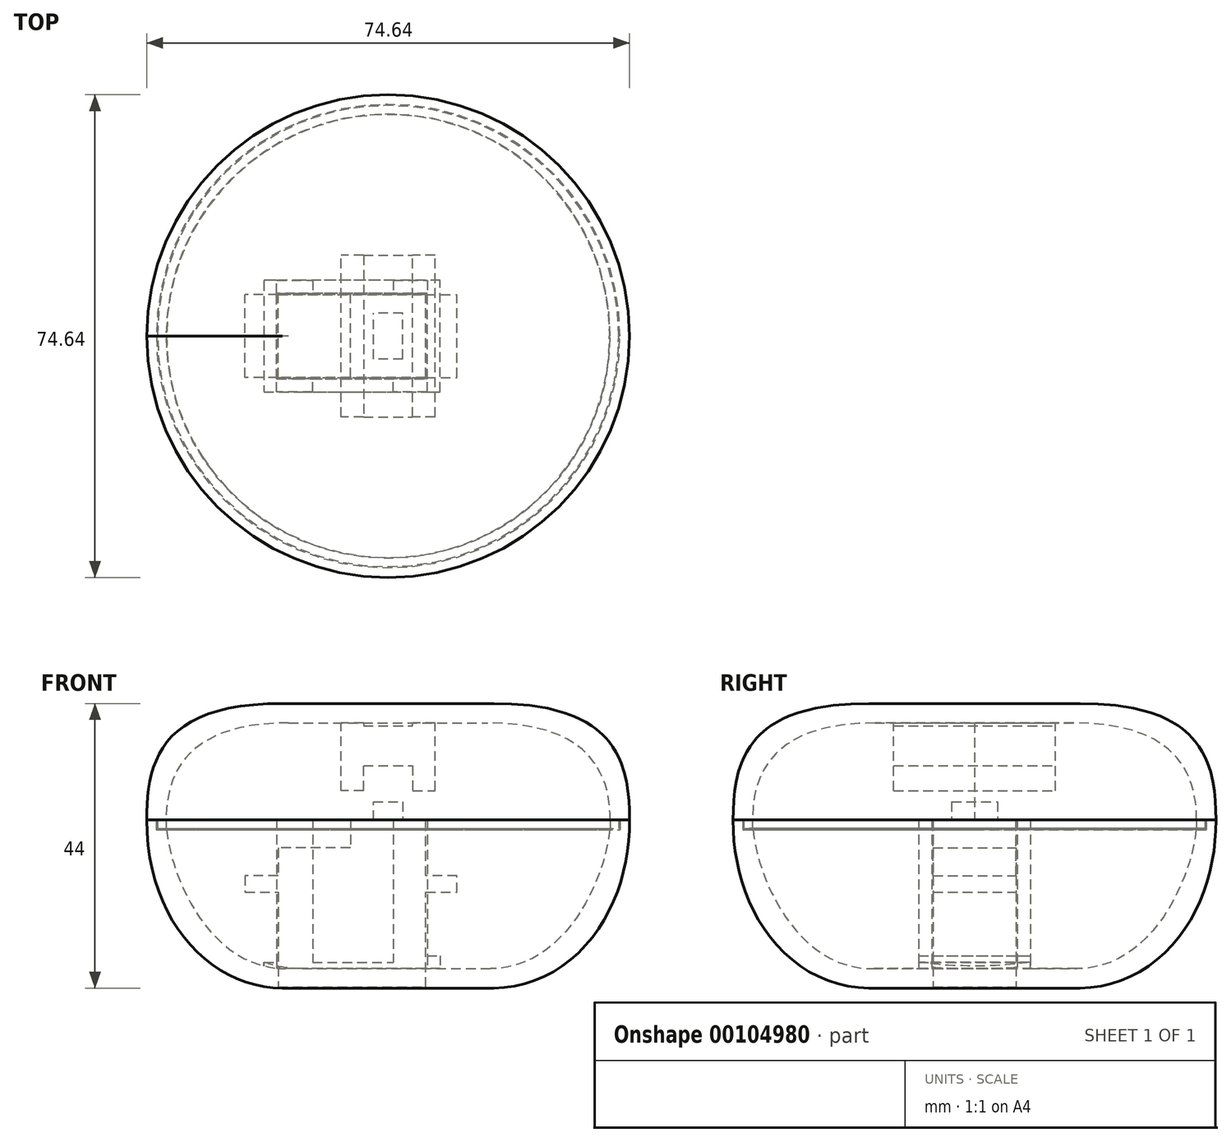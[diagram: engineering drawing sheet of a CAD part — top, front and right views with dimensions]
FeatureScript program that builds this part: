
annotation { "Feature Type Name" : "Feature", "Feature Type Description" : "" }
export const myFeature = defineFeature(function(context is Context, id is Id, definition is map)
    precondition{}
    {
        {
            var Q0;
            Q0=qCreatedBy(makeId("Front.planeOp"),FACE);
            var sketch = newSketch(context, id + "F0", { "sketchPlane" : qUnion([Q0])});
            skLineSegment(sketch, "E0", {"start": v(-62.74, 0) * mm, "end": v(62.74, 0) * mm, "construction": true});
            skLineSegment(sketch, "E1", {"start": v(0, -23) * mm, "end": v(15.82, -23) * mm});
            skFitSpline(sketch, "E2", {"points": [v(15.82, -23) * mm, v(34.32, 0) * mm], "startDerivative": vector(37, 0) * mm, "endDerivative": vector(0, 21.8) * mm});
            skLineSegment(sketch, "E3", {"start": v(0, -26) * mm, "end": v(16.32, -26) * mm});
            skFitSpline(sketch, "E4", {"points": [v(16.32, -26) * mm, v(37.32, 0) * mm], "startDerivative": vector(33.8, 0) * mm, "endDerivative": vector(0, 46.22) * mm});
            skLineSegment(sketch, "E5", {"start": v(0, -23) * mm, "end": v(0, -26) * mm});
            skLineSegment(sketch, "E6", {"start": v(34.32, 0) * mm, "end": v(37.32, 0) * mm});
            skLineSegment(sketch, "E7", {"start": v(35.82, 0) * mm, "end": v(35.82, -1.5) * mm});
            skLineSegment(sketch, "E8", {"start": v(35.82, -1.5) * mm, "end": v(34.25, -1.5) * mm});
            skLineSegment(sketch, "E9", {"start": v(37.32, 0) * mm, "end": v(37.32, 20.6) * mm, "construction": true});
            skSolve(sketch);
        }
        {
            var Q0;
            Q0=qCreatedBy(makeId("Front.planeOp"),FACE);
            var sketch = newSketch(context, id + "F1", { "sketchPlane" : qUnion([Q0])});
            skLineSegment(sketch, "E10", {"start": v(-17.02, -25.82) * mm, "end": v(5.84, -25.82) * mm});
            skLineSegment(sketch, "E11", {"start": v(5.84, -25.82) * mm, "end": v(5.84, -11.18) * mm});
            skLineSegment(sketch, "E12", {"start": v(5.84, -11.18) * mm, "end": v(10.67, -11.18) * mm});
            skLineSegment(sketch, "E13", {"start": v(10.67, -11.18) * mm, "end": v(10.67, -8.64) * mm});
            skLineSegment(sketch, "E14", {"start": v(10.67, -8.64) * mm, "end": v(5.84, -8.64) * mm});
            skLineSegment(sketch, "E15", {"start": v(5.84, -8.64) * mm, "end": v(5.84, 0) * mm});
            skLineSegment(sketch, "E16", {"start": v(5.84, 0) * mm, "end": v(-5.84, 0) * mm});
            skLineSegment(sketch, "E17", {"start": v(-5.84, 0) * mm, "end": v(-5.84, -4.32) * mm});
            skLineSegment(sketch, "E18", {"start": v(-5.84, -4.32) * mm, "end": v(-17.02, -4.32) * mm});
            skLineSegment(sketch, "E19", {"start": v(-17.02, -4.32) * mm, "end": v(-17.02, -8.64) * mm});
            skLineSegment(sketch, "E20", {"start": v(-17.02, -8.64) * mm, "end": v(-22.1, -8.64) * mm});
            skLineSegment(sketch, "E21", {"start": v(-22.1, -8.64) * mm, "end": v(-22.1, -11.18) * mm});
            skLineSegment(sketch, "E22", {"start": v(-22.1, -11.18) * mm, "end": v(-17.02, -11.18) * mm});
            skLineSegment(sketch, "E23", {"start": v(-17.02, -11.18) * mm, "end": v(-17.02, -25.82) * mm});
            skPoint(sketch, "E24", {"position": v(0, 0) * mm});
            skLineSegment(sketch, "E25", {"start": v(-2.29, 0) * mm, "end": v(-2.29, 2.8) * mm});
            skLineSegment(sketch, "E26", {"start": v(-2.29, 2.8) * mm, "end": v(2.29, 2.8) * mm});
            skLineSegment(sketch, "E27", {"start": v(2.29, 2.8) * mm, "end": v(2.29, 0) * mm});
            skLineSegment(sketch, "E28", {"start": v(0, 0) * mm, "end": v(0, 24.97) * mm, "construction": true});
            skSolve(sketch);
        }
        {
            var Q0;
            Q0=makeQuery(id+"F1.imprint","IMPRINT",FACE,{"disambiguationData":[TD([[makeQuery(id+"F1.imprint","IMPRINT",EDGE,{"derivedFrom":sQuery(id+"F1.wireOp",EDGE,"E10")}),1.0]])]});
            extrude(context, id + "F2", {"entities" : qUnion([Q0]), "endBound" : BoundingType.SYMMETRIC, "depth" : 12.83 * mm});
        }
        {
            var Q0;
            {var subQ0=sQuery(id+"F1.wireOp",EDGE,"E25");Q0=makeQuery(id+"F1.imprint","IMPRINT",FACE,{"disambiguationData":[TD([[makeQuery(id+"F1.imprint","IMPRINT",EDGE,{"derivedFrom":subQ0}),-1.0]])]});}
            extrude(context, id + "F3", {"entities" : qUnion([Q0]), "operationType" : NewBodyOperationType.ADD, "endBound" : BoundingType.SYMMETRIC, "depth" : 7.11 * mm});
        }
        {
            var Q0;
            Q0=makeQuery(id+"F0.imprint","IMPRINT",FACE,{"disambiguationData":[TD([[makeQuery(id+"F0.imprint","IMPRINT",EDGE,{"derivedFrom":sQuery(id+"F0.wireOp",EDGE,"E1")}),-1.0]])]});
            var Q1;
            Q1=sQuery(id+"F1.wireOp",EDGE,"E28");
            revolve(context, id + "F4", {"entities" : qUnion([Q0]), "axis" : qUnion([Q1]), "revolveType" : RevolveType.FULL});
        }
        {
            var Q0;
            Q0=makeQuery(id+"F4.opRevolve","SWEPT_FACE",FACE,{"disambiguationData":[OSD([sQuery(id+"F0.wireOp",EDGE,"E1")])]});
            var sketch = newSketch(context, id + "F5", { "sketchPlane" : qUnion([Q0])});
            skLineSegment(sketch, "E29", {"start": v(-17.22, -6.61) * mm, "end": v(6.04, -6.61) * mm});
            skLineSegment(sketch, "E30", {"start": v(6.04, -6.61) * mm, "end": v(6.04, 6.61) * mm});
            skLineSegment(sketch, "E31", {"start": v(6.04, 6.61) * mm, "end": v(-17.22, 6.61) * mm});
            skLineSegment(sketch, "E32", {"start": v(-17.22, 6.61) * mm, "end": v(-17.22, -6.61) * mm});
            skLineSegment(sketch, "E33", {"start": v(8.04, 8.61) * mm, "end": v(-19.22, 8.61) * mm});
            skLineSegment(sketch, "E34", {"start": v(-19.22, 8.61) * mm, "end": v(-19.22, -8.61) * mm});
            skLineSegment(sketch, "E35", {"start": v(-19.22, -8.61) * mm, "end": v(8.04, -8.61) * mm});
            skLineSegment(sketch, "E36", {"start": v(8.04, -8.61) * mm, "end": v(8.04, 8.61) * mm});
            skLineSegment(sketch, "E37", {"start": v(-17.22, -6.61) * mm, "end": v(-17.22, -8.61) * mm});
            skLineSegment(sketch, "E38", {"start": v(-11.68, -6.61) * mm, "end": v(-11.68, -8.61) * mm});
            skLineSegment(sketch, "E39", {"start": v(6.04, -6.61) * mm, "end": v(6.04, -8.61) * mm});
            skLineSegment(sketch, "E40", {"start": v(0.8, -6.61) * mm, "end": v(0.8, -8.61) * mm});
            skLineSegment(sketch, "E41", {"start": v(6.04, -6.61) * mm, "end": v(8.04, -6.61) * mm});
            skLineSegment(sketch, "E42", {"start": v(6.04, 6.61) * mm, "end": v(8.04, 6.61) * mm});
            skLineSegment(sketch, "E43", {"start": v(-17.22, 6.61) * mm, "end": v(-17.22, 8.61) * mm});
            skLineSegment(sketch, "E44", {"start": v(-11.68, 6.61) * mm, "end": v(-11.68, 8.61) * mm});
            skPoint(sketch, "E44.startSnap0", {"position": v(-11.68, -7.61) * mm});
            skLineSegment(sketch, "E45", {"start": v(0.8, 6.61) * mm, "end": v(0.8, 8.61) * mm});
            skLineSegment(sketch, "E46", {"start": v(6.04, 6.61) * mm, "end": v(6.04, 8.61) * mm});
            skSolve(sketch);
        }
        {
            var Q0;
            {var subQ0=sQuery(id+"F5.wireOp",EDGE,"E37");Q0=makeQuery(id+"F5.imprint","IMPRINT",FACE,{"disambiguationData":[TD([[makeQuery(id+"F5.imprint","IMPRINT",EDGE,{"derivedFrom":subQ0}),1.0]])]});}
            var Q1;
            {var subQ0=sQuery(id+"F5.wireOp",EDGE,"E38");Q1=makeQuery(id+"F5.imprint","IMPRINT",FACE,{"disambiguationData":[TD([[makeQuery(id+"F5.imprint","IMPRINT",EDGE,{"derivedFrom":subQ0}),-1.0]])]});}
            var Q2;
            {var subQ0=sQuery(id+"F5.wireOp",EDGE,"E39");Q2=makeQuery(id+"F5.imprint","IMPRINT",FACE,{"disambiguationData":[TD([[makeQuery(id+"F5.imprint","IMPRINT",EDGE,{"derivedFrom":subQ0}),-1.0]])]});}
            var Q3;
            {var subQ2=sQuery(id+"F5.wireOp",EDGE,"E45");Q3=makeQuery(id+"F5.imprint","IMPRINT",FACE,{"disambiguationData":[TD([[makeQuery(id+"F5.imprint","IMPRINT",EDGE,{"derivedFrom":subQ2}),-1.0]])]});}
            var Q4;
            {var subQ0=sQuery(id+"F5.wireOp",EDGE,"E44");Q4=makeQuery(id+"F5.imprint","IMPRINT",FACE,{"disambiguationData":[TD([[makeQuery(id+"F5.imprint","IMPRINT",EDGE,{"derivedFrom":subQ0}),1.0]])]});}
            var Q5;
            {var subQ0=sQuery(id+"F5.wireOp",EDGE,"E43");Q5=makeQuery(id+"F5.imprint","IMPRINT",FACE,{"disambiguationData":[TD([[makeQuery(id+"F5.imprint","IMPRINT",EDGE,{"derivedFrom":subQ0}),-1.0]])]});}
            var Q6;
            Q6=makeQuery(id+"F4.opRevolve","SWEPT_FACE",FACE,{"disambiguationData":[OSD([sQuery(id+"F0.wireOp",EDGE,"E6")])]});
            extrude(context, id + "F6", {"entities" : qUnion([Q0, Q1, Q2, Q3, Q4, Q5]), "operationType" : NewBodyOperationType.ADD, "endBound" : BoundingType.UP_TO_SURFACE, "endBoundEntityFace" : qUnion([Q6]), "depth" : 2.54 * mm});
        }
        {
            var Q0;
            Q0=qCreatedBy(makeId("Front.planeOp"),FACE);
            var sketch = newSketch(context, id + "F7", { "sketchPlane" : qUnion([Q0])});
            skLineSegment(sketch, "E47", {"start": v(0, 18) * mm, "end": v(16.32, 18) * mm});
            skLineSegment(sketch, "E48", {"start": v(0, 15) * mm, "end": v(15.4, 15) * mm});
            skLineSegment(sketch, "E49", {"start": v(0, 15) * mm, "end": v(0, 18) * mm});
            skFitSpline(sketch, "E50", {"points": [v(15.4, 15) * mm, v(34.32, 0) * mm], "startDerivative": vector(49.1, 0) * mm, "endDerivative": vector(0, -19.41) * mm});
            skFitSpline(sketch, "E51", {"points": [v(16.32, 18) * mm, v(37.32, 0) * mm], "startDerivative": vector(55.9, 0) * mm, "endDerivative": vector(0, -28.06) * mm});
            skLineSegment(sketch, "E52", {"start": v(16.32, 30.13) * mm, "end": v(16.32, -30.66) * mm, "construction": true});
            skLineSegment(sketch, "E53", {"start": v(34.32, 0) * mm, "end": v(37.32, 0) * mm});
            skLineSegment(sketch, "E54", {"start": v(35.66, 0) * mm, "end": v(35.66, -1.35) * mm});
            skLineSegment(sketch, "E55", {"start": v(35.66, -1.35) * mm, "end": v(34.32, -1.35) * mm});
            skLineSegment(sketch, "E56", {"start": v(34.32, -1.35) * mm, "end": v(34.32, 0) * mm});
            skSolve(sketch);
        }
        {
            var Q0;
            Q0 = qSketchRegion(id + "F7", true);
            var Q1;
            Q1=sQuery(id+"F1.wireOp",EDGE,"E28");
            revolve(context, id + "F8", {"entities" : qUnion([Q0]), "axis" : qUnion([Q1]), "revolveType" : RevolveType.FULL});
        }
        {
            var Q0;
            Q0=qCreatedBy(makeId("Front.planeOp"),FACE);
            var sketch = newSketch(context, id + "F9", { "sketchPlane" : qUnion([Q0])});
            skLineSegment(sketch, "E57", {"start": v(-3.8, 4.53) * mm, "end": v(-3.8, 8.38) * mm});
            skLineSegment(sketch, "E58", {"start": v(-3.8, 8.38) * mm, "end": v(3.81, 8.38) * mm});
            skLineSegment(sketch, "E59", {"start": v(3.81, 8.38) * mm, "end": v(3.81, 4.53) * mm});
            skLineSegment(sketch, "E60", {"start": v(3.81, 4.53) * mm, "end": v(7.27, 4.53) * mm});
            skLineSegment(sketch, "E61", {"start": v(7.27, 4.53) * mm, "end": v(7.27, 17.05) * mm});
            skLineSegment(sketch, "E62", {"start": v(-3.8, 4.53) * mm, "end": v(-7.27, 4.53) * mm});
            skLineSegment(sketch, "E63", {"start": v(-7.27, 4.53) * mm, "end": v(-7.27, 17.05) * mm});
            skLineSegment(sketch, "E64", {"start": v(-3.8, 17.05) * mm, "end": v(-3.8, 14.52) * mm});
            skLineSegment(sketch, "E65", {"start": v(-3.8, 14.52) * mm, "end": v(3.81, 14.52) * mm});
            skLineSegment(sketch, "E66", {"start": v(3.81, 14.52) * mm, "end": v(3.81, 17.05) * mm});
            skLineSegment(sketch, "E67", {"start": v(-7.27, 17.05) * mm, "end": v(-3.81, 17.05) * mm});
            skLineSegment(sketch, "E68", {"start": v(3.81, 17.05) * mm, "end": v(7.27, 17.05) * mm});
            skSolve(sketch);
        }
        {
            var Q0;
            Q0=makeQuery(id+"F9.imprint","IMPRINT",FACE,{"disambiguationData":[TD([[makeQuery(id+"F9.imprint","IMPRINT",EDGE,{"derivedFrom":sQuery(id+"F9.wireOp",EDGE,"E57")}),1.0]])]});
            extrude(context, id + "F10", {"entities" : qUnion([Q0]), "operationType" : NewBodyOperationType.ADD, "endBound" : BoundingType.SYMMETRIC, "depth" : 25 * mm});
        }
        {
            var Q0;
            Q0=makeQuery(id+"F5.imprint","IMPRINT",FACE,{"disambiguationData":[TD([[makeQuery(id+"F5.imprint","IMPRINT",EDGE,{"derivedFrom":sQuery(id+"F5.wireOp",EDGE,"E30")}),-1.0]])]});
            var Q1;
            {var subQ3=sQuery(id+"F5.wireOp",EDGE,"E39");Q1=makeQuery(id+"F5.imprint","IMPRINT",FACE,{"disambiguationData":[TD([[makeQuery(id+"F5.imprint","IMPRINT",EDGE,{"derivedFrom":subQ3}),1.0]])]});}
            var Q2;
            {var subQ4=sQuery(id+"F5.wireOp",EDGE,"E42");Q2=makeQuery(id+"F5.imprint","IMPRINT",FACE,{"disambiguationData":[TD([[makeQuery(id+"F5.imprint","IMPRINT",EDGE,{"derivedFrom":subQ4}),1.0]])]});}
            extrude(context, id + "F11", {"entities" : qUnion([Q0, Q1, Q2]), "operationType" : NewBodyOperationType.ADD, "depth" : 2 * mm});
        }
        {
            var Q0;
            {var subQ0=sQuery(id+"F5.wireOp",EDGE,"E38");Q0=makeQuery(id+"F5.imprint","IMPRINT",FACE,{"disambiguationData":[TD([[makeQuery(id+"F5.imprint","IMPRINT",EDGE,{"derivedFrom":subQ0}),1.0]])]});}
            var Q1;
            {var subQ0=sQuery(id+"F5.wireOp",EDGE,"E44");Q1=makeQuery(id+"F5.imprint","IMPRINT",FACE,{"disambiguationData":[TD([[makeQuery(id+"F5.imprint","IMPRINT",EDGE,{"derivedFrom":subQ0}),-1.0]])]});}
            var Q2;
            Q2=makeQuery(id+"F5.imprint","IMPRINT",FACE,{"disambiguationData":[TD([[makeQuery(id+"F5.imprint","IMPRINT",EDGE,{"derivedFrom":sQuery(id+"F5.wireOp",EDGE,"E32")}),-1.0]])]});
            extrude(context, id + "F12", {"entities" : qUnion([Q0, Q1, Q2]), "operationType" : NewBodyOperationType.ADD, "depth" : 1 * mm});
        }
    });
